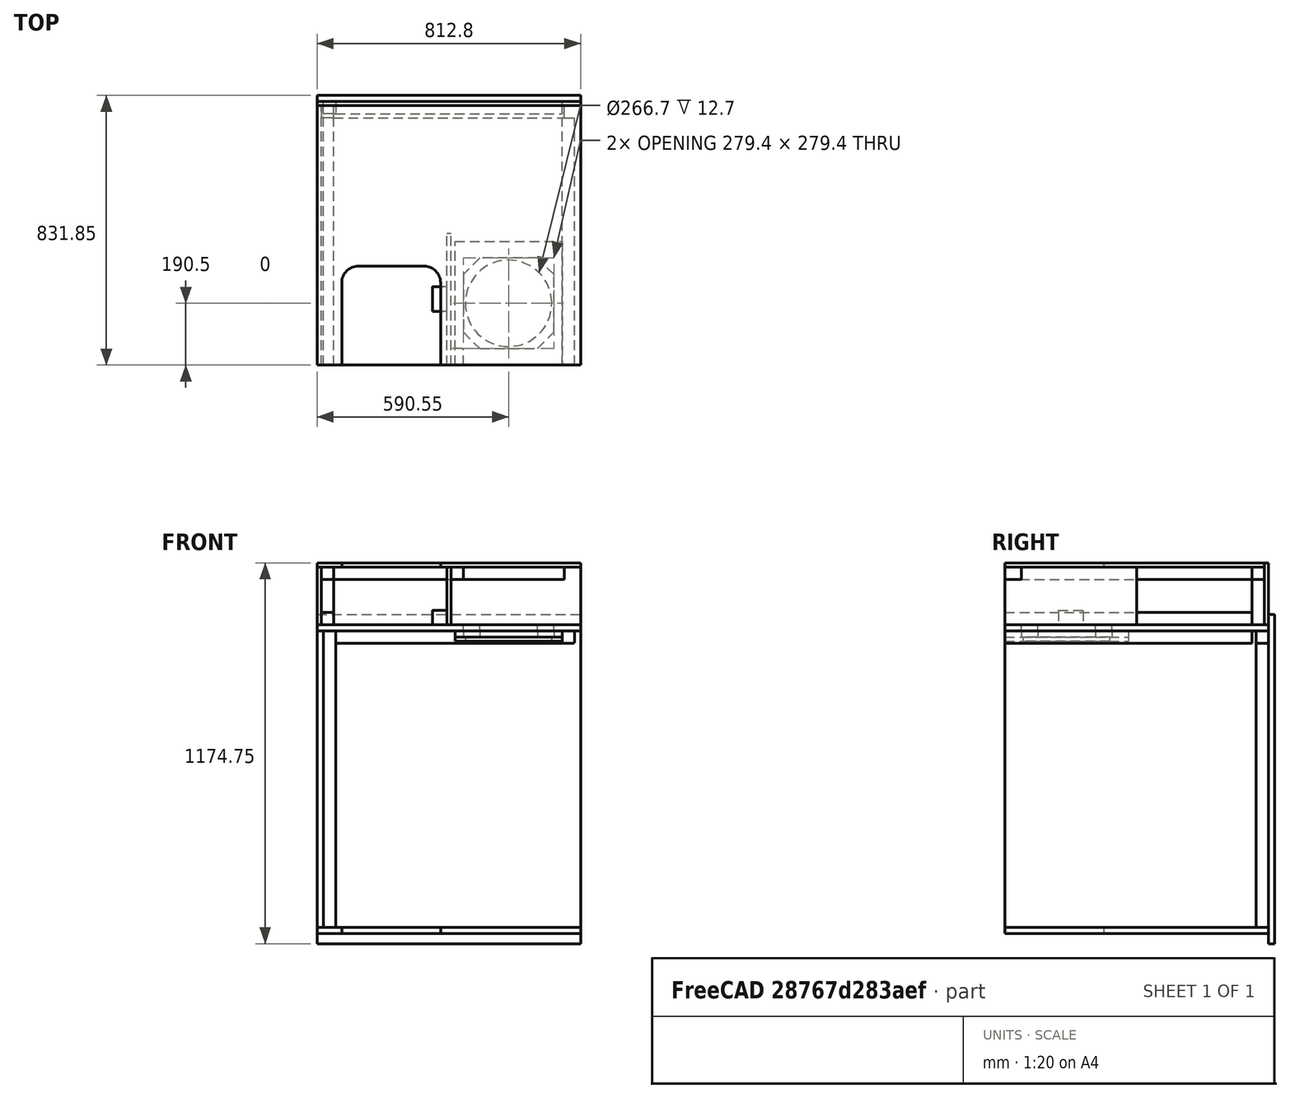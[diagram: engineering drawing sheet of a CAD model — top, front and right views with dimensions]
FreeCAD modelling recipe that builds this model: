
FCSTD DOCUMENT  (FreeCAD 0.19R)
Label: GenBox
License: Creative Commons Attribution
LicenseURL: http://creativecommons.org/licenses/by/4.0/
objects: App::Link×28, Sketcher::SketchObject×19, Part::Extrusion×19, Part::Feature×1, App::LinkGroup×1, Mesh::Feature×1
note: 39 computed .brp shape members not serialized (recipe doc carries the construction recipe); baked Part::Feature solids carry a one-line shape summary decoded from their .brp

FEATURE [Sketcher::SketchObject] Sketch004  label="Sketch_H_Inlet_Wall"
  sketch-geometry (12):
    g0: LineSegment StartX=0 StartY=0 StartZ=0 EndX=812.8 EndY=0 EndZ=0
    g1: LineSegment StartX=812.8 StartY=0 StartZ=0 EndX=812.8 EndY=812.8 EndZ=0
    g2: LineSegment StartX=812.8 StartY=812.8 StartZ=0 EndX=0 EndY=812.8 EndZ=0
    g3: LineSegment StartX=0 StartY=812.8 StartZ=0 EndX=0 EndY=0 EndZ=0
    g4: LineSegment StartX=730.25 StartY=101.6 StartZ=0 EndX=730.25 EndY=279.4 EndZ=0
    g5: LineSegment StartX=730.25 StartY=279.4 StartZ=0 EndX=679.45 EndY=330.2 EndZ=0
    g6: LineSegment StartX=679.45 StartY=330.2 StartZ=0 EndX=501.65 EndY=330.2 EndZ=0
    g7: LineSegment StartX=501.65 StartY=330.2 StartZ=0 EndX=450.85 EndY=279.4 EndZ=0
    g8: LineSegment StartX=450.85 StartY=279.4 StartZ=0 EndX=450.85 EndY=101.6 EndZ=0
    g9: LineSegment StartX=450.85 StartY=101.6 StartZ=0 EndX=501.65 EndY=50.8 EndZ=0
    g10: LineSegment StartX=501.65 StartY=50.8 StartZ=0 EndX=679.45 EndY=50.8 EndZ=0
    g11: LineSegment StartX=679.45 StartY=50.8 StartZ=0 EndX=730.25 EndY=101.6 EndZ=0
  constraints (35):
    c: Coincident(g0,g1)
    c: Coincident(g1,g2)
    c: Coincident(g2,g3)
    c: Coincident(g3,g0)
    c: Horizontal(g0)
    c: Horizontal(g2)
    c: Vertical(g1)
    c: Vertical(g3)
    c: Coincident(g0,g-1)
    c: DistanceX(g0,g0) = 812.8
    c: DistanceY(g3,g3) = 812.8
    c: Vertical(g4)
    c: Coincident(g4,g5)
    c: Coincident(g5,g6)
    c: Horizontal(g6)
    c: Coincident(g6,g7)
    c: Coincident(g7,g8)
    c: Vertical(g8)
    c: Coincident(g8,g9)
    c: Coincident(g9,g10)
    c: Horizontal(g10)
    c: Coincident(g10,g11)
    c: Coincident(g11,g4)
    c: DistanceX(g4,g0) = 82.55
    c: DistanceY(g0,g10) = 50.8
    c: DistanceX(g8,g9) = 50.8
    c: Perpendicular(g7,g9)
    c: DistanceX(g8,g4) = 279.4
    c: Equal(g8,g6)
    c: Equal(g6,g4)
    c: Equal(g4,g10)
    c: Equal(g9,g7)
    c: Equal(g7,g5)
    c: Equal(g5,g11)
    c: DistanceY(g9,g8) = 50.8
FEATURE [Part::Extrusion] Extrude004  label="Part_H_Inlet_Wall"
  Base = -> Sketch004
  Dir = (0,0,1)
  DirMode = 2
  FaceMakerClass = Part::FaceMakerBullseye
  LengthFwd = 19.05
  LengthRev = 0
  Solid = true
  Symmetric = false
FEATURE [Sketcher::SketchObject] Sketch005  label="Sketch_I_Fan_Mount"
  sketch-geometry (5):
    g0: LineSegment StartX=0 StartY=0 StartZ=0 EndX=330.2 EndY=0 EndZ=0
    g1: LineSegment StartX=330.2 StartY=0 StartZ=0 EndX=330.2 EndY=381 EndZ=0
    g2: LineSegment StartX=330.2 StartY=381 StartZ=0 EndX=0 EndY=381 EndZ=0
    g3: LineSegment StartX=0 StartY=381 StartZ=0 EndX=0 EndY=0 EndZ=0
    g4: Circle CenterX=165.1 CenterY=190.5 CenterZ=0 NormalX=0 NormalY=0 NormalZ=1 AngleXU=0 Radius=133.35
  constraints (13):
    c: Coincident(g0,g1)
    c: Coincident(g1,g2)
    c: Coincident(g2,g3)
    c: Coincident(g3,g0)
    c: Horizontal(g0)
    c: Horizontal(g2)
    c: Vertical(g1)
    c: Vertical(g3)
    c: Coincident(g0,g-1)
    c: DistanceY(g3,g3) = 381
    c: DistanceX(g0,g0) = 330.2
    c: Diameter(g4) = 266.7
    c: Symmetric(g0,g1,g4)
FEATURE [Part::Extrusion] Extrude005  label="Part_I_Fan_Mount"
  Base = -> Sketch005
  Dir = (0,0,1)
  DirMode = 2
  FaceMakerClass = Part::FaceMakerBullseye
  LengthFwd = 12.7
  LengthRev = 0
  Placement = pos=(755.65,0,-19.05) rot=(0,1,0;3.14159rad)
  Solid = true
  Symmetric = false
FEATURE [Part::Feature] Part__Feature  label="FAN_W2E250-HJ32-01"
  Placement = pos=(590.55,190.5,-19.05) rot=(-1,0,0;4.71239rad)
  shape: bbox 300.2 x 295.3 x 80.4 mm, 902 faces, 0 solids (baked)
FEATURE [Sketcher::SketchObject] Sketch006  label="Sketch_2x2_rail"
  sketch-geometry (8):
    g0: LineSegment StartX=0 StartY=34.925 StartZ=0 EndX=0 EndY=3.175 EndZ=0
    g1: ArcOfCircle CenterX=3.175 CenterY=34.925 CenterZ=0 NormalX=0 NormalY=0 NormalZ=1 AngleXU=0 Radius=3.175 StartAngle=1.5708 EndAngle=3.14159
    g2: LineSegment StartX=3.175 StartY=38.1 StartZ=0 EndX=34.925 EndY=38.1 EndZ=0
    g3: ArcOfCircle CenterX=34.925 CenterY=34.925 CenterZ=0 NormalX=0 NormalY=0 NormalZ=1 AngleXU=0 Radius=3.175 StartAngle=4e-16 EndAngle=1.5708
    g4: LineSegment StartX=38.1 StartY=34.925 StartZ=0 EndX=38.1 EndY=3.175 EndZ=0
    g5: ArcOfCircle CenterX=34.925 CenterY=3.175 CenterZ=0 NormalX=0 NormalY=0 NormalZ=1 AngleXU=0 Radius=3.175 StartAngle=4.71239 EndAngle=6.28319
    g6: LineSegment StartX=34.925 StartY=0 StartZ=0 EndX=3.175 EndY=0 EndZ=0
    g7: ArcOfCircle CenterX=3.175 CenterY=3.175 CenterZ=0 NormalX=0 NormalY=0 NormalZ=1 AngleXU=0 Radius=3.175 StartAngle=3.14159 EndAngle=4.71239
  constraints (22):
    c: Vertical(g0)
    c: Tangent(g0,g1) = -1.5708
    c: Radius(g1) = 3.175
    c: Angle(g1) = 1.5708
    c: Coincident(g2,g1)
    c: Horizontal(g2)
    c: Tangent(g2,g3) = 1.5708
    c: Coincident(g4,g3)
    c: Vertical(g4)
    c: Tangent(g5,g4) = 1.5708
    c: Horizontal(g6)
    c: Tangent(g6,g5) = 1.5708
    c: Tangent(g7,g6) = 1.5708
    c: Tangent(g7,g0) = -1.5708
    c: Equal(g1,g7)
    c: Equal(g7,g3)
    c: Equal(g2,g0)
    c: Equal(g0,g6)
    c: Equal(g6,g4)
    c: PointOnObject(g-1,g0)
    c: PointOnObject(g6,g-1)
    c: DistanceX(g0,g4) = 38.1
FEATURE [Part::Extrusion] Extrude006  label="IF_A"
  Base = -> Sketch006
  Dir = (0,0,1)
  DirMode = 2
  FaceMakerClass = Part::FaceMakerBullseye
  LengthFwd = 762
  LengthRev = 0
  Placement = pos=(793.75,0,9.9e-15) rot=(-0.57735,0.57735,0.57735;2.0944rad)
  Solid = true
  Symmetric = false
FEATURE [Sketcher::SketchObject] Sketch007  label="Sketch_H_Inlet_Wall001"
  sketch-geometry (12):
    g0: LineSegment StartX=0 StartY=0 StartZ=0 EndX=330.2 EndY=0 EndZ=0
    g1: LineSegment StartX=330.2 StartY=0 StartZ=0 EndX=330.2 EndY=381 EndZ=0
    g2: LineSegment StartX=330.2 StartY=381 StartZ=0 EndX=0 EndY=381 EndZ=0
    g3: LineSegment StartX=0 StartY=381 StartZ=0 EndX=0 EndY=0 EndZ=0
    g4: LineSegment StartX=304.8 StartY=101.6 StartZ=0 EndX=304.8 EndY=279.4 EndZ=0
    g5: LineSegment StartX=304.8 StartY=279.4 StartZ=0 EndX=254 EndY=330.2 EndZ=0
    g6: LineSegment StartX=254 StartY=330.2 StartZ=0 EndX=76.2 EndY=330.2 EndZ=0
    g7: LineSegment StartX=76.2 StartY=330.2 StartZ=0 EndX=25.4 EndY=279.4 EndZ=0
    g8: LineSegment StartX=25.4 StartY=279.4 StartZ=0 EndX=25.4 EndY=101.6 EndZ=0
    g9: LineSegment StartX=25.4 StartY=101.6 StartZ=0 EndX=76.2 EndY=50.8 EndZ=0
    g10: LineSegment StartX=76.2 StartY=50.8 StartZ=0 EndX=254 EndY=50.8 EndZ=0
    g11: LineSegment StartX=254 StartY=50.8 StartZ=0 EndX=304.8 EndY=101.6 EndZ=0
  constraints (35):
    c: Coincident(g0,g1)
    c: Coincident(g1,g2)
    c: Coincident(g2,g3)
    c: Coincident(g3,g0)
    c: Horizontal(g0)
    c: Horizontal(g2)
    c: Vertical(g1)
    c: Vertical(g3)
    c: Coincident(g0,g-1)
    c: DistanceX(g0,g0) = 330.2
    c: DistanceY(g3,g3) = 381
    c: Vertical(g4)
    c: Coincident(g4,g5)
    c: Coincident(g5,g6)
    c: Horizontal(g6)
    c: Coincident(g6,g7)
    c: Coincident(g7,g8)
    c: Vertical(g8)
    c: Coincident(g8,g9)
    c: Coincident(g9,g10)
    c: Horizontal(g10)
    c: Coincident(g10,g11)
    c: Coincident(g11,g4)
    c: DistanceX(g7,g4) = 279.4
    c: DistanceX(g4,g0) = 25.4
    c: DistanceY(g0,g10) = 50.8
    c: DistanceX(g8,g9) = 50.8
    c: Perpendicular(g11,g9)
    c: Equal(g6,g10)
    c: Equal(g10,g8)
    c: Equal(g8,g4)
    c: Equal(g7,g11)
    c: Equal(g11,g9)
    c: Equal(g9,g5)
    c: DistanceY(g9,g8) = 50.8
FEATURE [Part::Extrusion] Extrude007  label="Fan_Spacer"
  Base = -> Sketch007
  Dir = (0,0,1)
  DirMode = 2
  FaceMakerClass = Part::FaceMakerBullseye
  LengthFwd = 19.05
  LengthRev = 0
  Placement = pos=(755.65,0,4.16e-14) rot=(0,1,0;3.14159rad)
  Solid = true
  Symmetric = false
FEATURE [Sketcher::SketchObject] Sketch  label="Sketch_2x2_rail001"
  sketch-geometry (8):
    g0: LineSegment StartX=0 StartY=34.925 StartZ=0 EndX=0 EndY=3.175 EndZ=0
    g1: ArcOfCircle CenterX=3.175 CenterY=34.925 CenterZ=0 NormalX=0 NormalY=0 NormalZ=1 AngleXU=0 Radius=3.175 StartAngle=1.5708 EndAngle=3.14159
    g2: LineSegment StartX=3.175 StartY=38.1 StartZ=0 EndX=34.925 EndY=38.1 EndZ=0
    g3: ArcOfCircle CenterX=34.925 CenterY=34.925 CenterZ=0 NormalX=0 NormalY=0 NormalZ=1 AngleXU=0 Radius=3.175 StartAngle=2.2e-15 EndAngle=1.5708
    g4: LineSegment StartX=38.1 StartY=34.925 StartZ=0 EndX=38.1 EndY=3.175 EndZ=0
    g5: ArcOfCircle CenterX=34.925 CenterY=3.175 CenterZ=0 NormalX=0 NormalY=0 NormalZ=1 AngleXU=0 Radius=3.175 StartAngle=4.71239 EndAngle=6.28319
    g6: LineSegment StartX=34.925 StartY=0 StartZ=0 EndX=3.175 EndY=0 EndZ=0
    g7: ArcOfCircle CenterX=3.175 CenterY=3.175 CenterZ=0 NormalX=0 NormalY=0 NormalZ=1 AngleXU=0 Radius=3.175 StartAngle=3.14159 EndAngle=4.71239
  constraints (22):
    c: Vertical(g0)
    c: Tangent(g0,g1) = -1.5708
    c: Radius(g1) = 3.175
    c: Angle(g1) = 1.5708
    c: Coincident(g2,g1)
    c: Horizontal(g2)
    c: Tangent(g2,g3) = 1.5708
    c: Coincident(g4,g3)
    c: Vertical(g4)
    c: Tangent(g5,g4) = 1.5708
    c: Horizontal(g6)
    c: Tangent(g6,g5) = 1.5708
    c: Tangent(g7,g6) = 1.5708
    c: Tangent(g7,g0) = -1.5708
    c: Equal(g1,g7)
    c: Equal(g7,g3)
    c: Equal(g2,g0)
    c: Equal(g0,g6)
    c: Equal(g6,g4)
    c: PointOnObject(g-1,g0)
    c: PointOnObject(g6,g-1)
    c: DistanceX(g0,g4) = 38.1
FEATURE [Part::Extrusion] Extrude  label="BF_A"
  Base = -> Sketch
  Dir = (0,0,1)
  DirMode = 2
  FaceMakerClass = Part::FaceMakerBullseye
  LengthFwd = 800.1
  LengthRev = 0
  Placement = pos=(12.7,4.4e-14,196.85) rot=(-1,0,0;1.5708rad)
  Solid = true
  Symmetric = false
FEATURE [Sketcher::SketchObject] Sketch008  label="Sketch_D_Baffle_Ext_Wall"
  sketch-geometry (10):
    g0: LineSegment StartX=0 StartY=0 StartZ=0 EndX=0 EndY=800.1 EndZ=0
    g1: LineSegment StartX=0 StartY=800.1 StartZ=0 EndX=812.8 EndY=800.1 EndZ=0
    g2: LineSegment StartX=812.8 StartY=800.1 StartZ=0 EndX=812.8 EndY=0 EndZ=0
    g3: LineSegment StartX=812.8 StartY=0 StartZ=0 EndX=736.6 EndY=0 EndZ=0
    g4: LineSegment StartX=736.6 StartY=0 StartZ=0 EndX=736.6 EndY=254 EndZ=0
    g5: LineSegment StartX=685.8 StartY=304.8 StartZ=0 EndX=482.6 EndY=304.8 EndZ=0
    g6: LineSegment StartX=431.8 StartY=254 StartZ=0 EndX=431.8 EndY=0 EndZ=0
    g7: LineSegment StartX=431.8 StartY=0 StartZ=0 EndX=0 EndY=0 EndZ=0
    g8: ArcOfCircle CenterX=482.6 CenterY=254 CenterZ=0 NormalX=0 NormalY=0 NormalZ=1 AngleXU=0 Radius=50.8 StartAngle=1.5708 EndAngle=3.14159
    g9: ArcOfCircle CenterX=685.8 CenterY=254 CenterZ=0 NormalX=0 NormalY=0 NormalZ=1 AngleXU=0 Radius=50.8 StartAngle=0 EndAngle=1.5708
  constraints (27):
    c: Coincident(g-1,g0)
    c: PointOnObject(g0,g-2)
    c: Coincident(g0,g1)
    c: Horizontal(g1)
    c: Coincident(g1,g2)
    c: PointOnObject(g2,g-1)
    c: Vertical(g2)
    c: Coincident(g2,g3)
    c: PointOnObject(g3,g-1)
    c: Coincident(g3,g4)
    c: Vertical(g4)
    c: Horizontal(g5)
    c: PointOnObject(g6,g-1)
    c: Vertical(g6)
    c: Coincident(g6,g7)
    c: Coincident(g7,g0)
    c: DistanceY(g0,g0) = 800.1
    c: DistanceX(g1,g1) = 812.8
    c: DistanceX(g3,g3) = 76.2
    c: DistanceX(g6,g3) = 304.8
    c: DistanceY(g6,g5) = 304.8
    c: Equal(g8,g9)
    c: Tangent(g8,g6) = -1.5708
    c: Tangent(g9,g4) = -1.5708
    c: Tangent(g9,g5) = -1.5708
    c: Tangent(g8,g5) = -1.5708
    c: Radius(g8) = 50.8
FEATURE [Part::Extrusion] Extrude008  label="Part_D_Baffle_Ext_Wall_001"
  Base = -> Sketch008
  Dir = (0,0,1)
  DirMode = 2
  FaceMakerClass = Part::FaceMakerBullseye
  LengthFwd = 12.7
  LengthRev = 0
  Placement = pos=(812.8,0,209.55) rot=(0,1,0;3.14159rad)
  Solid = true
  Symmetric = false
FEATURE [Sketcher::SketchObject] Sketch009  label="Sketch_G_Baffle_Half_Wall"
  sketch-geometry (4):
    g0: LineSegment StartX=0 StartY=0 StartZ=0 EndX=406.4 EndY=0 EndZ=0
    g1: LineSegment StartX=406.4 StartY=0 StartZ=0 EndX=406.4 EndY=177.8 EndZ=0
    g2: LineSegment StartX=406.4 StartY=177.8 StartZ=0 EndX=0 EndY=177.8 EndZ=0
    g3: LineSegment StartX=0 StartY=177.8 StartZ=0 EndX=0 EndY=0 EndZ=0
  constraints (11):
    c: Coincident(g0,g1)
    c: Coincident(g1,g2)
    c: Coincident(g2,g3)
    c: Coincident(g3,g0)
    c: Horizontal(g0)
    c: Horizontal(g2)
    c: Vertical(g1)
    c: Vertical(g3)
    c: Coincident(g0,g-1)
    c: DistanceY(g3,g3) = 177.8
    c: DistanceX(g0,g0) = 406.4
FEATURE [Part::Extrusion] Extrude009  label="Part_G_Baffle_Half_Wall_001"
  Base = -> Sketch009
  Dir = (0,0,1)
  DirMode = 2
  FaceMakerClass = Part::FaceMakerBullseye
  LengthFwd = 12.7
  LengthRev = 0
  Placement = pos=(400.05,-8.5e-14,19.05) rot=(0.57735,0.57735,0.57735;2.0944rad)
  Solid = true
  Symmetric = false
FEATURE [Sketcher::SketchObject] Sketch010  label="Sketch_E_Baffle_Top"
  sketch-geometry (4):
    g0: LineSegment StartX=0 StartY=0 StartZ=0 EndX=812.8 EndY=0 EndZ=0
    g1: LineSegment StartX=812.8 StartY=0 StartZ=0 EndX=812.8 EndY=190.5 EndZ=0
    g2: LineSegment StartX=812.8 StartY=190.5 StartZ=0 EndX=0 EndY=190.5 EndZ=0
    g3: LineSegment StartX=0 StartY=190.5 StartZ=0 EndX=0 EndY=0 EndZ=0
  constraints (11):
    c: Coincident(g0,g1)
    c: Coincident(g1,g2)
    c: Coincident(g2,g3)
    c: Coincident(g3,g0)
    c: Horizontal(g0)
    c: Horizontal(g2)
    c: Vertical(g1)
    c: Vertical(g3)
    c: Coincident(g0,g-1)
    c: DistanceY(g3,g3) = 190.5
    c: DistanceX(g0,g0) = 812.8
FEATURE [Part::Extrusion] Extrude010  label="Part_E_Baffle_Top_001"
  Base = -> Sketch010
  Dir = (0,0,1)
  DirMode = 2
  FaceMakerClass = Part::FaceMakerBullseye
  LengthFwd = 12.7
  LengthRev = 0
  Placement = pos=(0,812.8,19.05) rot=(1,0,0;1.5708rad)
  Solid = true
  Symmetric = false
FEATURE [Sketcher::SketchObject] Sketch012  label="Sketch_F_Baffle_Side_Wall"
  sketch-geometry (4):
    g0: LineSegment StartX=0 StartY=0 StartZ=0 EndX=800.1 EndY=0 EndZ=0
    g1: LineSegment StartX=800.1 StartY=0 StartZ=0 EndX=800.1 EndY=177.8 EndZ=0
    g2: LineSegment StartX=800.1 StartY=177.8 StartZ=0 EndX=0 EndY=177.8 EndZ=0
    g3: LineSegment StartX=0 StartY=177.8 StartZ=0 EndX=0 EndY=0 EndZ=0
  constraints (11):
    c: Coincident(g0,g1)
    c: Coincident(g1,g2)
    c: Coincident(g2,g3)
    c: Coincident(g3,g0)
    c: Horizontal(g0)
    c: Horizontal(g2)
    c: Vertical(g1)
    c: Vertical(g3)
    c: Coincident(g0,g-1)
    c: DistanceY(g3,g3) = 177.8
    c: DistanceX(g0,g0) = 800.1
FEATURE [Part::Extrusion] Extrude012  label="Part_F_Baffle_Side_Wall_001"
  Base = -> Sketch012
  Dir = (0,0,1)
  DirMode = 2
  FaceMakerClass = Part::FaceMakerBullseye
  LengthFwd = 12.7
  LengthRev = 0
  Placement = pos=(-4e-15,-8e-15,19.05) rot=(0.57735,0.57735,0.57735;2.0944rad)
  Solid = true
  Symmetric = false
FEATURE [Sketcher::SketchObject] Sketch013  label="Sketch_2x2_rail002"
  sketch-geometry (8):
    g0: LineSegment StartX=0 StartY=34.925 StartZ=0 EndX=0 EndY=3.175 EndZ=0
    g1: ArcOfCircle CenterX=3.175 CenterY=34.925 CenterZ=0 NormalX=0 NormalY=0 NormalZ=1 AngleXU=0 Radius=3.175 StartAngle=1.5708 EndAngle=3.14159
    g2: LineSegment StartX=3.175 StartY=38.1 StartZ=0 EndX=34.925 EndY=38.1 EndZ=0
    g3: ArcOfCircle CenterX=34.925 CenterY=34.925 CenterZ=0 NormalX=0 NormalY=0 NormalZ=1 AngleXU=0 Radius=3.175 StartAngle=1.1e-15 EndAngle=1.5708
    g4: LineSegment StartX=38.1 StartY=34.925 StartZ=0 EndX=38.1 EndY=3.175 EndZ=0
    g5: ArcOfCircle CenterX=34.925 CenterY=3.175 CenterZ=0 NormalX=0 NormalY=0 NormalZ=1 AngleXU=0 Radius=3.175 StartAngle=4.71239 EndAngle=6.28319
    g6: LineSegment StartX=34.925 StartY=4e-16 StartZ=0 EndX=3.175 EndY=4e-16 EndZ=0
    g7: ArcOfCircle CenterX=3.175 CenterY=3.175 CenterZ=0 NormalX=0 NormalY=0 NormalZ=1 AngleXU=0 Radius=3.175 StartAngle=3.14159 EndAngle=4.71239
  constraints (22):
    c: Vertical(g0)
    c: Tangent(g0,g1) = -1.5708
    c: Radius(g1) = 3.175
    c: Angle(g1) = 1.5708
    c: Coincident(g2,g1)
    c: Horizontal(g2)
    c: Tangent(g2,g3) = 1.5708
    c: Coincident(g4,g3)
    c: Vertical(g4)
    c: Tangent(g5,g4) = 1.5708
    c: Horizontal(g6)
    c: Tangent(g6,g5) = 1.5708
    c: Tangent(g7,g6) = 1.5708
    c: Tangent(g7,g0) = -1.5708
    c: Equal(g1,g7)
    c: Equal(g7,g3)
    c: Equal(g2,g0)
    c: Equal(g0,g6)
    c: Equal(g6,g4)
    c: PointOnObject(g-1,g0)
    c: PointOnObject(g6,g-1)
    c: DistanceX(g0,g4) = 38.1
FEATURE [Part::Extrusion] Extrude013  label="BF_C"
  Base = -> Sketch013
  Dir = (0,0,1)
  DirMode = 2
  FaceMakerClass = Part::FaceMakerBullseye
  LengthFwd = 139.7
  LengthRev = 0
  Placement = pos=(12.7,762,19.05) rot=(0,0,1;0rad)
  Solid = true
  Symmetric = false
FEATURE [Sketcher::SketchObject] Sketch014  label="Sketch_2x2_rail003"
  sketch-geometry (8):
    g0: LineSegment StartX=0 StartY=34.925 StartZ=0 EndX=0 EndY=3.175 EndZ=0
    g1: ArcOfCircle CenterX=3.175 CenterY=34.925 CenterZ=0 NormalX=0 NormalY=0 NormalZ=1 AngleXU=0 Radius=3.175 StartAngle=1.5708 EndAngle=3.14159
    g2: LineSegment StartX=3.175 StartY=38.1 StartZ=0 EndX=34.925 EndY=38.1 EndZ=0
    g3: ArcOfCircle CenterX=34.925 CenterY=34.925 CenterZ=0 NormalX=0 NormalY=0 NormalZ=1 AngleXU=0 Radius=3.175 StartAngle=9e-16 EndAngle=1.5708
    g4: LineSegment StartX=38.1 StartY=34.925 StartZ=0 EndX=38.1 EndY=3.175 EndZ=0
    g5: ArcOfCircle CenterX=34.925 CenterY=3.175 CenterZ=0 NormalX=0 NormalY=0 NormalZ=1 AngleXU=0 Radius=3.175 StartAngle=4.71239 EndAngle=6.28319
    g6: LineSegment StartX=34.925 StartY=4e-16 StartZ=0 EndX=3.175 EndY=4e-16 EndZ=0
    g7: ArcOfCircle CenterX=3.175 CenterY=3.175 CenterZ=0 NormalX=0 NormalY=0 NormalZ=1 AngleXU=0 Radius=3.175 StartAngle=3.14159 EndAngle=4.71239
  constraints (22):
    c: Vertical(g0)
    c: Tangent(g0,g1) = -1.5708
    c: Radius(g1) = 3.175
    c: Angle(g1) = 1.5708
    c: Coincident(g2,g1)
    c: Horizontal(g2)
    c: Tangent(g2,g3) = 1.5708
    c: Coincident(g4,g3)
    c: Vertical(g4)
    c: Tangent(g5,g4) = 1.5708
    c: Horizontal(g6)
    c: Tangent(g6,g5) = 1.5708
    c: Tangent(g7,g6) = 1.5708
    c: Tangent(g7,g0) = -1.5708
    c: Equal(g1,g7)
    c: Equal(g7,g3)
    c: Equal(g2,g0)
    c: Equal(g0,g6)
    c: Equal(g6,g4)
    c: PointOnObject(g-1,g0)
    c: PointOnObject(g6,g-1)
    c: DistanceX(g0,g4) = 38.1
FEATURE [Part::Extrusion] Extrude014  label="BF_B"
  Base = -> Sketch014
  Dir = (0,0,1)
  DirMode = 2
  FaceMakerClass = Part::FaceMakerBullseye
  LengthFwd = 711.2
  LengthRev = 0
  Placement = pos=(50.8,800.1,196.85) rot=(0.57735,-0.57735,0.57735;4.18879rad)
  Solid = true
  Symmetric = false
FEATURE [Sketcher::SketchObject] Sketch015  label="Sketch_2x2_rail004"
  sketch-geometry (8):
    g0: LineSegment StartX=0 StartY=34.925 StartZ=0 EndX=0 EndY=3.175 EndZ=0
    g1: ArcOfCircle CenterX=3.175 CenterY=34.925 CenterZ=0 NormalX=0 NormalY=0 NormalZ=1 AngleXU=0 Radius=3.175 StartAngle=1.5708 EndAngle=3.14159
    g2: LineSegment StartX=3.175 StartY=38.1 StartZ=0 EndX=34.925 EndY=38.1 EndZ=0
    g3: ArcOfCircle CenterX=34.925 CenterY=34.925 CenterZ=0 NormalX=0 NormalY=0 NormalZ=1 AngleXU=0 Radius=3.175 StartAngle=1.2e-15 EndAngle=1.5708
    g4: LineSegment StartX=38.1 StartY=34.925 StartZ=0 EndX=38.1 EndY=3.175 EndZ=0
    g5: ArcOfCircle CenterX=34.925 CenterY=3.175 CenterZ=0 NormalX=0 NormalY=0 NormalZ=1 AngleXU=0 Radius=3.175 StartAngle=4.71239 EndAngle=6.28319
    g6: LineSegment StartX=34.925 StartY=0 StartZ=0 EndX=3.175 EndY=0 EndZ=0
    g7: ArcOfCircle CenterX=3.175 CenterY=3.175 CenterZ=0 NormalX=0 NormalY=0 NormalZ=1 AngleXU=0 Radius=3.175 StartAngle=3.14159 EndAngle=4.71239
  constraints (22):
    c: Vertical(g0)
    c: Tangent(g0,g1) = -1.5708
    c: Radius(g1) = 3.175
    c: Angle(g1) = 1.5708
    c: Coincident(g2,g1)
    c: Horizontal(g2)
    c: Tangent(g2,g3) = 1.5708
    c: Coincident(g4,g3)
    c: Vertical(g4)
    c: Tangent(g5,g4) = 1.5708
    c: Horizontal(g6)
    c: Tangent(g6,g5) = 1.5708
    c: Tangent(g7,g6) = 1.5708
    c: Tangent(g7,g0) = -1.5708
    c: Equal(g1,g7)
    c: Equal(g7,g3)
    c: Equal(g2,g0)
    c: Equal(g0,g6)
    c: Equal(g6,g4)
    c: PointOnObject(g-1,g0)
    c: PointOnObject(g6,g-1)
    c: DistanceX(g0,g4) = 38.1
FEATURE [Part::Extrusion] Extrude015  label="BF_D"
  Base = -> Sketch015
  Dir = (0,0,1)
  DirMode = 2
  FaceMakerClass = Part::FaceMakerBullseye
  LengthFwd = 762
  LengthRev = 0
  Placement = pos=(12.7,2.39e-14,19.05) rot=(0.57735,0.57735,0.57735;4.18879rad)
  Solid = true
  Symmetric = false
FEATURE [Sketcher::SketchObject] Sketch016  label="Sketch_2x2_rail005"
  sketch-geometry (8):
    g0: LineSegment StartX=0 StartY=34.925 StartZ=0 EndX=0 EndY=3.175 EndZ=0
    g1: ArcOfCircle CenterX=3.175 CenterY=34.925 CenterZ=0 NormalX=0 NormalY=0 NormalZ=1 AngleXU=0 Radius=3.175 StartAngle=1.5708 EndAngle=3.14159
    g2: LineSegment StartX=3.175 StartY=38.1 StartZ=0 EndX=34.925 EndY=38.1 EndZ=0
    g3: ArcOfCircle CenterX=34.925 CenterY=34.925 CenterZ=0 NormalX=0 NormalY=0 NormalZ=1 AngleXU=0 Radius=3.175 StartAngle=2.5e-15 EndAngle=1.5708
    g4: LineSegment StartX=38.1 StartY=34.925 StartZ=0 EndX=38.1 EndY=3.175 EndZ=0
    g5: ArcOfCircle CenterX=34.925 CenterY=3.175 CenterZ=0 NormalX=0 NormalY=0 NormalZ=1 AngleXU=0 Radius=3.175 StartAngle=4.71239 EndAngle=6.28319
    g6: LineSegment StartX=34.925 StartY=4e-16 StartZ=0 EndX=3.175 EndY=4e-16 EndZ=0
    g7: ArcOfCircle CenterX=3.175 CenterY=3.175 CenterZ=0 NormalX=0 NormalY=0 NormalZ=1 AngleXU=0 Radius=3.175 StartAngle=3.14159 EndAngle=4.71239
  constraints (22):
    c: Vertical(g0)
    c: Tangent(g0,g1) = -1.5708
    c: Radius(g1) = 3.175
    c: Angle(g1) = 1.5708
    c: Coincident(g2,g1)
    c: Horizontal(g2)
    c: Tangent(g2,g3) = 1.5708
    c: Coincident(g4,g3)
    c: Vertical(g4)
    c: Tangent(g5,g4) = 1.5708
    c: Horizontal(g6)
    c: Tangent(g6,g5) = 1.5708
    c: Tangent(g7,g6) = 1.5708
    c: Tangent(g7,g0) = -1.5708
    c: Equal(g1,g7)
    c: Equal(g7,g3)
    c: Equal(g2,g0)
    c: Equal(g0,g6)
    c: Equal(g6,g4)
    c: PointOnObject(g-1,g0)
    c: PointOnObject(g6,g-1)
    c: DistanceX(g0,g4) = 38.1
FEATURE [Part::Extrusion] Extrude016  label="BF_E"
  Base = -> Sketch016
  Dir = (0,0,1)
  DirMode = 2
  FaceMakerClass = Part::FaceMakerBullseye
  LengthFwd = 50.8
  LengthRev = 0
  Placement = pos=(412.75,8.8e-14,196.85) rot=(-1,0,0;1.5708rad)
  Solid = true
  Symmetric = false
FEATURE [Sketcher::SketchObject] Sketch017  label="Sketch_2x2_rail006"
  sketch-geometry (8):
    g0: LineSegment StartX=0 StartY=41.275 StartZ=0 EndX=0 EndY=3.175 EndZ=0
    g1: ArcOfCircle CenterX=3.175 CenterY=41.275 CenterZ=0 NormalX=0 NormalY=0 NormalZ=1 AngleXU=0 Radius=3.175 StartAngle=1.5708 EndAngle=3.14159
    g2: LineSegment StartX=3.175 StartY=44.45 StartZ=0 EndX=41.275 EndY=44.45 EndZ=0
    g3: ArcOfCircle CenterX=41.275 CenterY=41.275 CenterZ=0 NormalX=0 NormalY=0 NormalZ=1 AngleXU=0 Radius=3.175 StartAngle=-9e-16 EndAngle=1.5708
    g4: LineSegment StartX=44.45 StartY=41.275 StartZ=0 EndX=44.45 EndY=3.175 EndZ=0
    g5: ArcOfCircle CenterX=41.275 CenterY=3.175 CenterZ=0 NormalX=0 NormalY=0 NormalZ=1 AngleXU=0 Radius=3.175 StartAngle=4.71239 EndAngle=6.28319
    g6: LineSegment StartX=41.275 StartY=1.3e-15 StartZ=0 EndX=3.175 EndY=1.3e-15 EndZ=0
    g7: ArcOfCircle CenterX=3.175 CenterY=3.175 CenterZ=0 NormalX=0 NormalY=0 NormalZ=1 AngleXU=0 Radius=3.175 StartAngle=3.14159 EndAngle=4.71239
  constraints (22):
    c: Vertical(g0)
    c: Tangent(g0,g1) = -1.5708
    c: Radius(g1) = 3.175
    c: Angle(g1) = 1.5708
    c: Coincident(g2,g1)
    c: Horizontal(g2)
    c: Tangent(g2,g3) = 1.5708
    c: Coincident(g4,g3)
    c: Vertical(g4)
    c: Tangent(g5,g4) = 1.5708
    c: Horizontal(g6)
    c: Tangent(g6,g5) = 1.5708
    c: Tangent(g7,g6) = 1.5708
    c: Tangent(g7,g0) = -1.5708
    c: Equal(g1,g7)
    c: Equal(g7,g3)
    c: Equal(g2,g0)
    c: Equal(g0,g6)
    c: Equal(g6,g4)
    c: PointOnObject(g-1,g0)
    c: PointOnObject(g6,g-1)
    c: DistanceX(g0,g4) = 44.45
FEATURE [Part::Extrusion] Extrude017  label="BF_F"
  Base = -> Sketch017
  Dir = (0,0,1)
  DirMode = 2
  FaceMakerClass = Part::FaceMakerBullseye
  LengthFwd = 76.2
  LengthRev = 0
  Placement = pos=(400.05,165.1,19.05) rot=(0,-0.707107,-0.707107;3.14159rad)
  Solid = true
  Symmetric = false
FEATURE [Sketcher::SketchObject] Sketch018  label="Sketch_A"
  sketch-geometry (4):
    g0: LineSegment StartX=0 StartY=0 StartZ=0 EndX=812.8 EndY=0 EndZ=0
    g1: LineSegment StartX=812.8 StartY=0 StartZ=0 EndX=812.8 EndY=1016 EndZ=0
    g2: LineSegment StartX=812.8 StartY=1016 StartZ=0 EndX=0 EndY=1016 EndZ=0
    g3: LineSegment StartX=0 StartY=1016 StartZ=0 EndX=0 EndY=0 EndZ=0
  constraints (11):
    c: Coincident(g0,g1)
    c: Coincident(g1,g2)
    c: Coincident(g2,g3)
    c: Coincident(g3,g0)
    c: Horizontal(g0)
    c: Horizontal(g2)
    c: Vertical(g1)
    c: Vertical(g3)
    c: Coincident(g0,g-1)
    c: Distance(g0) = 812.8
    c: Distance(g1) = 1016
FEATURE [Part::Extrusion] Extrude018  label="Part_A_Lid"
  Base = -> Sketch018
  Dir = (0,0,1)
  DirMode = 2
  FaceMakerClass = Part::FaceMakerBullseye
  LengthFwd = 19.05
  LengthRev = 0
  Placement = pos=(0,812.8,50.8) rot=(-1,0,0;1.5708rad)
  Solid = true
  Symmetric = false
FEATURE [Sketcher::SketchObject] Sketch019  label="Sketch_2x2_rail007"
  sketch-geometry (8):
    g0: LineSegment StartX=0 StartY=34.925 StartZ=0 EndX=0 EndY=3.175 EndZ=0
    g1: ArcOfCircle CenterX=3.175 CenterY=34.925 CenterZ=0 NormalX=0 NormalY=0 NormalZ=1 AngleXU=0 Radius=3.175 StartAngle=1.5708 EndAngle=3.14159
    g2: LineSegment StartX=3.175 StartY=38.1 StartZ=0 EndX=34.925 EndY=38.1 EndZ=0
    g3: ArcOfCircle CenterX=34.925 CenterY=34.925 CenterZ=0 NormalX=0 NormalY=0 NormalZ=1 AngleXU=0 Radius=3.175 StartAngle=1.2e-15 EndAngle=1.5708
    g4: LineSegment StartX=38.1 StartY=34.925 StartZ=0 EndX=38.1 EndY=3.175 EndZ=0
    g5: ArcOfCircle CenterX=34.925 CenterY=3.175 CenterZ=0 NormalX=0 NormalY=0 NormalZ=1 AngleXU=0 Radius=3.175 StartAngle=4.71239 EndAngle=6.28319
    g6: LineSegment StartX=34.925 StartY=0 StartZ=0 EndX=3.175 EndY=0 EndZ=0
    g7: ArcOfCircle CenterX=3.175 CenterY=3.175 CenterZ=0 NormalX=0 NormalY=0 NormalZ=1 AngleXU=0 Radius=3.175 StartAngle=3.14159 EndAngle=4.71239
  constraints (22):
    c: Vertical(g0)
    c: Tangent(g0,g1) = -1.5708
    c: Radius(g1) = 3.175
    c: Angle(g1) = 1.5708
    c: Coincident(g2,g1)
    c: Horizontal(g2)
    c: Tangent(g2,g3) = 1.5708
    c: Coincident(g4,g3)
    c: Vertical(g4)
    c: Tangent(g5,g4) = 1.5708
    c: Horizontal(g6)
    c: Tangent(g6,g5) = 1.5708
    c: Tangent(g7,g6) = 1.5708
    c: Tangent(g7,g0) = -1.5708
    c: Equal(g1,g7)
    c: Equal(g7,g3)
    c: Equal(g2,g0)
    c: Equal(g0,g6)
    c: Equal(g6,g4)
    c: PointOnObject(g-1,g0)
    c: PointOnObject(g6,g-1)
    c: DistanceX(g0,g4) = 38.1
FEATURE [Part::Extrusion] Extrude019  label="LF_A"
  Base = -> Sketch019
  Dir = (0,0,1)
  DirMode = 2
  FaceMakerClass = Part::FaceMakerBullseye
  LengthFwd = 914.4
  LengthRev = 0
  Placement = pos=(19.05,812.8,-914.4) rot=(0,0,1;4.71239rad)
  Solid = true
  Symmetric = false
FEATURE [Sketcher::SketchObject] Sketch020  label="Sketch_2x2_rail008"
  sketch-geometry (8):
    g0: LineSegment StartX=0 StartY=34.925 StartZ=0 EndX=0 EndY=3.175 EndZ=0
    g1: ArcOfCircle CenterX=3.175 CenterY=34.925 CenterZ=0 NormalX=0 NormalY=0 NormalZ=1 AngleXU=0 Radius=3.175 StartAngle=1.5708 EndAngle=3.14159
    g2: LineSegment StartX=3.175 StartY=38.1 StartZ=0 EndX=34.925 EndY=38.1 EndZ=0
    g3: ArcOfCircle CenterX=34.925 CenterY=34.925 CenterZ=0 NormalX=0 NormalY=0 NormalZ=1 AngleXU=0 Radius=3.175 StartAngle=1.5e-15 EndAngle=1.5708
    g4: LineSegment StartX=38.1 StartY=34.925 StartZ=0 EndX=38.1 EndY=3.175 EndZ=0
    g5: ArcOfCircle CenterX=34.925 CenterY=3.175 CenterZ=0 NormalX=0 NormalY=0 NormalZ=1 AngleXU=0 Radius=3.175 StartAngle=4.71239 EndAngle=6.28319
    g6: LineSegment StartX=34.925 StartY=4e-16 StartZ=0 EndX=3.175 EndY=4e-16 EndZ=0
    g7: ArcOfCircle CenterX=3.175 CenterY=3.175 CenterZ=0 NormalX=0 NormalY=0 NormalZ=1 AngleXU=0 Radius=3.175 StartAngle=3.14159 EndAngle=4.71239
  constraints (22):
    c: Vertical(g0)
    c: Tangent(g0,g1) = -1.5708
    c: Radius(g1) = 3.175
    c: Angle(g1) = 1.5708
    c: Coincident(g2,g1)
    c: Horizontal(g2)
    c: Tangent(g2,g3) = 1.5708
    c: Coincident(g4,g3)
    c: Vertical(g4)
    c: Tangent(g5,g4) = 1.5708
    c: Horizontal(g6)
    c: Tangent(g6,g5) = 1.5708
    c: Tangent(g7,g6) = 1.5708
    c: Tangent(g7,g0) = -1.5708
    c: Equal(g1,g7)
    c: Equal(g7,g3)
    c: Equal(g2,g0)
    c: Equal(g0,g6)
    c: Equal(g6,g4)
    c: PointOnObject(g-1,g0)
    c: PointOnObject(g6,g-1)
    c: DistanceX(g0,g4) = 38.1
FEATURE [Part::Extrusion] Extrude020  label="LF_B"
  Base = -> Sketch020
  Dir = (0,0,1)
  DirMode = 2
  FaceMakerClass = Part::FaceMakerBullseye
  LengthFwd = 698.5
  LengthRev = 0
  Placement = pos=(57.15,812.8,2.8e-15) rot=(0.57735,-0.57735,0.57735;4.18879rad)
  Solid = true
  Symmetric = false
FEATURE [App::Link] Link  label="IF_A001"
  LinkPlacement = pos=(19.05,2.707e-13,2.27094e-06) rot=(-1,0,0;1.5708rad)
  LinkedObject = -> Extrude006
  Placement = pos=(19.05,2.707e-13,2.27094e-06) rot=(-1,0,0;1.5708rad)
FEATURE [App::Link] Link001  label="Part_F_Baffle_Side_Wall_002"
  LinkPlacement = pos=(800.1,9.59848e-05,19.0499) rot=(0.57735,0.57735,0.57735;2.0944rad)
  LinkedObject = -> Extrude012
  Placement = pos=(800.1,9.59848e-05,19.0499) rot=(0.57735,0.57735,0.57735;2.0944rad)
FEATURE [App::Link] Link002  label="BF_A001"
  LinkPlacement = pos=(762,2.34664e-05,196.85) rot=(-1,0,0;1.5708rad)
  LinkedObject = -> Extrude
  Placement = pos=(762,2.34664e-05,196.85) rot=(-1,0,0;1.5708rad)
FEATURE [App::Link] Link003  label="BF_B001"
  LinkPlacement = pos=(50.8,762,19.05) rot=(0.57735,0.57735,0.57735;2.0944rad)
  LinkedObject = -> Extrude014
  Placement = pos=(50.8,762,19.05) rot=(0.57735,0.57735,0.57735;2.0944rad)
FEATURE [App::Link] Link004  label="BF_C001"
  LinkPlacement = pos=(800.1,800.1,19.05) rot=(0,0,1;3.14159rad)
  LinkedObject = -> Extrude013
  Placement = pos=(800.1,800.1,19.05) rot=(0,0,1;3.14159rad)
FEATURE [App::Link] Link005  label="BF_D001"
  LinkPlacement = pos=(800.1,-5.29885e-06,19.0501) rot=(0,0.707107,0.707107;3.14159rad)
  LinkedObject = -> Extrude015
  Placement = pos=(800.1,-5.29885e-06,19.0501) rot=(0,0.707107,0.707107;3.14159rad)
FEATURE [App::Link] Link006  label="BF_E001"
  LinkPlacement = pos=(400.05,406.4,196.85) rot=(0,-0.707107,0.707107;3.14159rad)
  LinkedObject = -> Extrude016
  Placement = pos=(400.05,406.4,196.85) rot=(0,-0.707107,0.707107;3.14159rad)
FEATURE [App::Link] Link007  label="Part_G_Baffle_Half_Wall_002"
  LinkTransform = true
  LinkedObject = -> Extrude009
FEATURE [App::Link] Link008  label="Part_F_Baffle_Side_Wall_003"
  LinkTransform = true
  LinkedObject = -> Extrude012
FEATURE [App::Link] Link009  label="Part_F_Baffle_Side_Wall_004"
  LinkTransform = true
  LinkedObject = -> Link001
FEATURE [App::Link] Link010  label="Part_E_Baffle_Top_002"
  LinkTransform = true
  LinkedObject = -> Extrude010
FEATURE [App::Link] Link011  label="BF_A002"
  LinkTransform = true
  LinkedObject = -> Extrude
FEATURE [App::Link] Link012  label="BF_A003"
  LinkTransform = true
  LinkedObject = -> Link002
FEATURE [App::Link] Link013  label="BF_B002"
  LinkTransform = true
  LinkedObject = -> Extrude014
FEATURE [App::Link] Link014  label="BF_B003"
  LinkTransform = true
  LinkedObject = -> Link003
FEATURE [App::Link] Link015  label="BF_C002"
  LinkTransform = true
  LinkedObject = -> Extrude013
FEATURE [App::Link] Link016  label="BF_C003"
  LinkTransform = true
  LinkedObject = -> Link004
FEATURE [App::Link] Link017  label="Part_D_Baffle_Ext_Wall_002"
  LinkTransform = true
  LinkedObject = -> Extrude008
FEATURE [App::Link] Link018  label="BF_D002"
  LinkTransform = true
  LinkedObject = -> Extrude015
FEATURE [App::Link] Link019  label="BF_D003"
  LinkPlacement = pos=(-1.137e-13,-1.07055e-05,-0.00106049) rot=(-1,0,0;0rad)
  LinkTransform = true
  LinkedObject = -> Link005
  Placement = pos=(-1.137e-13,-1.07055e-05,-0.00106049) rot=(-1,0,0;0rad)
FEATURE [App::Link] Link020  label="BF_E002"
  LinkTransform = true
  LinkedObject = -> Extrude016
FEATURE [App::Link] Link021  label="BF_E003"
  LinkTransform = true
  LinkedObject = -> Link006
FEATURE [App::Link] Link022  label="BF_F001"
  LinkTransform = true
  LinkedObject = -> Extrude017
FEATURE [App::LinkGroup] LinkGroup  label="Outlet_Baffle"
  ElementList = -> [Link007,Link008,Link009,Link010,Link011,Link012,Link013,Link014,Link015,Link016,Link017,Link018,Link020,Link021,Link022,Link019]
  LinkMode = 1
  Placement = pos=(812.8,0.000288684,-914.401) rot=(0,1,0;3.14159rad)
FEATURE [Sketcher::SketchObject] Sketch003  label="Sketch_C_Outlet_Wall"
  sketch-geometry (10):
    g0: LineSegment StartX=812.8 StartY=812.8 StartZ=0 EndX=0 EndY=812.8 EndZ=0
    g1: LineSegment StartX=0 StartY=812.8 StartZ=0 EndX=0 EndY=0 EndZ=0
    g2: LineSegment StartX=0 StartY=0 StartZ=0 EndX=431.8 EndY=0 EndZ=0
    g3: LineSegment StartX=812.8 StartY=0 StartZ=0 EndX=812.8 EndY=812.8 EndZ=0
    g4: LineSegment StartX=812.8 StartY=0 StartZ=0 EndX=736.6 EndY=0 EndZ=0
    g5: LineSegment StartX=482.6 StartY=304.8 StartZ=0 EndX=685.8 EndY=304.8 EndZ=0
    g6: LineSegment StartX=431.8 StartY=0 StartZ=0 EndX=431.8 EndY=254 EndZ=0
    g7: LineSegment StartX=736.6 StartY=0 StartZ=0 EndX=736.6 EndY=254 EndZ=0
    g8: ArcOfCircle CenterX=482.6 CenterY=254 CenterZ=0 NormalX=0 NormalY=0 NormalZ=1 AngleXU=0 Radius=50.8 StartAngle=1.5708 EndAngle=3.14159
    g9: ArcOfCircle CenterX=685.8 CenterY=254 CenterZ=0 NormalX=0 NormalY=0 NormalZ=1 AngleXU=0 Radius=50.8 StartAngle=0 EndAngle=1.5708
  constraints (32):
    c: Coincident(g0,g1)
    c: Coincident(g2,g1)
    c: Coincident(g3,g0)
    c: DistanceX(g1) = 0
    c: DistanceY(g1) = 0
    c: Vertical(g0,g1)
    c: Vertical(g0,g3)
    c: Horizontal(g0,g0)
    c: DistanceY(g1,g0) = 812.8
    c: DistanceX(g0,g0) = 812.8
    c: Horizontal(g2)
    c: Coincident(g4,g3)
    c: PointOnObject(g4,g-1)
    c: Horizontal(g4)
    c: Horizontal(g5)
    c: DistanceX(g2,g4) = 304.8
    c: DistanceX(g4,g4) = 76.2
    c: DistanceY(g2,g5) = 304.8
    c: Coincident(g6,g2)
    c: Vertical(g6)
    c: Coincident(g7,g4)
    c: Vertical(g7)
    c: Equal(g6,g7)
    c: Coincident(g8,g5)
    c: Coincident(g8,g6)
    c: Coincident(g9,g5)
    c: Coincident(g9,g7)
    c: Horizontal(g6,g8)
    c: Vertical(g8,g5)
    c: Horizontal(g9,g7)
    c: Vertical(g9,g5)
    c: DistanceX(g6,g8) = 50.8
FEATURE [Part::Extrusion] Extrude003  label="Part_C_Outlet_Wall"
  Base = -> Sketch003
  Dir = (0,0,1)
  DirMode = 2
  FaceMakerClass = Part::FaceMakerBullseye
  LengthFwd = 19.05
  LengthRev = 0
  Placement = pos=(812.8,0,-914.4) rot=(0,1,0;3.14159rad)
  Solid = true
  Symmetric = false
FEATURE [App::Link] Link023  label="IF_A002"
  LinkPlacement = pos=(19.05,-0.000104463,-876.301) rot=(-1,0,0;1.5708rad)
  LinkedObject = -> Extrude006
  Placement = pos=(19.05,-0.000104463,-876.301) rot=(-1,0,0;1.5708rad)
FEATURE [App::Link] Link024  label="IF_A003"
  LinkPlacement = pos=(793.75,-5.05915e-05,-914.4) rot=(0,0.707107,0.707107;3.14159rad)
  LinkedObject = -> Extrude006
  Placement = pos=(793.75,-5.05915e-05,-914.4) rot=(0,0.707107,0.707107;3.14159rad)
FEATURE [Sketcher::SketchObject] Sketch001  label="Sketch_B"
  sketch-geometry (4):
    g0: LineSegment StartX=0 StartY=0 StartZ=0 EndX=812.8 EndY=0 EndZ=0
    g1: LineSegment StartX=812.8 StartY=0 StartZ=0 EndX=812.8 EndY=914.4 EndZ=0
    g2: LineSegment StartX=812.8 StartY=914.4 StartZ=0 EndX=0 EndY=914.4 EndZ=0
    g3: LineSegment StartX=0 StartY=914.4 StartZ=0 EndX=0 EndY=0 EndZ=0
  constraints (11):
    c: Coincident(g0,g1)
    c: Coincident(g1,g2)
    c: Coincident(g2,g3)
    c: Coincident(g3,g0)
    c: Horizontal(g0)
    c: Horizontal(g2)
    c: Vertical(g1)
    c: Vertical(g3)
    c: Distance(g0) = 812.8
    c: Distance(g1) = 914.4
    c: Coincident(g-1,g0)
FEATURE [Part::Extrusion] Extrude001  label="Part_B_Side_Wall_001"
  Base = -> Sketch001
  Dir = (0,0,1)
  DirMode = 2
  FaceMakerClass = Part::FaceMakerBullseye
  LengthFwd = 19.05
  LengthRev = 0
  Placement = pos=(8.1e-14,7.6e-14,-914.4) rot=(0.57735,0.57735,0.57735;2.0944rad)
  Solid = true
  Symmetric = false
FEATURE [App::Link] Link025  label="Part_B_Side_Wall_002"
  LinkPlacement = pos=(793.75,1.66536e-05,-914.4) rot=(0.57735,0.57735,0.57735;2.0944rad)
  LinkedObject = -> Extrude001
  Placement = pos=(793.75,1.66536e-05,-914.4) rot=(0.57735,0.57735,0.57735;2.0944rad)
FEATURE [App::Link] Link026  label="LF_A001"
  LinkPlacement = pos=(793.75,812.8,-914.4) rot=(0,0,1;3.14159rad)
  LinkedObject = -> Extrude019
  Placement = pos=(793.75,812.8,-914.4) rot=(0,0,1;3.14159rad)
FEATURE [App::Link] Link027  label="LF_B001"
  LinkPlacement = pos=(57.1499,812.8,-914.4) rot=(0.707107,0,0.707107;3.14159rad)
  LinkedObject = -> Extrude020
  Placement = pos=(57.1499,812.8,-914.4) rot=(0.707107,0,0.707107;3.14159rad)
FEATURE [Mesh::Feature] _6582_5500W_Portable_Gas_Generator_v1  label="16582_5500W_Portable_Gas_Generator_v1"
  Placement = pos=(412.75,2.806e-13,-476.25) rot=(1,0,0;4.71239rad)
